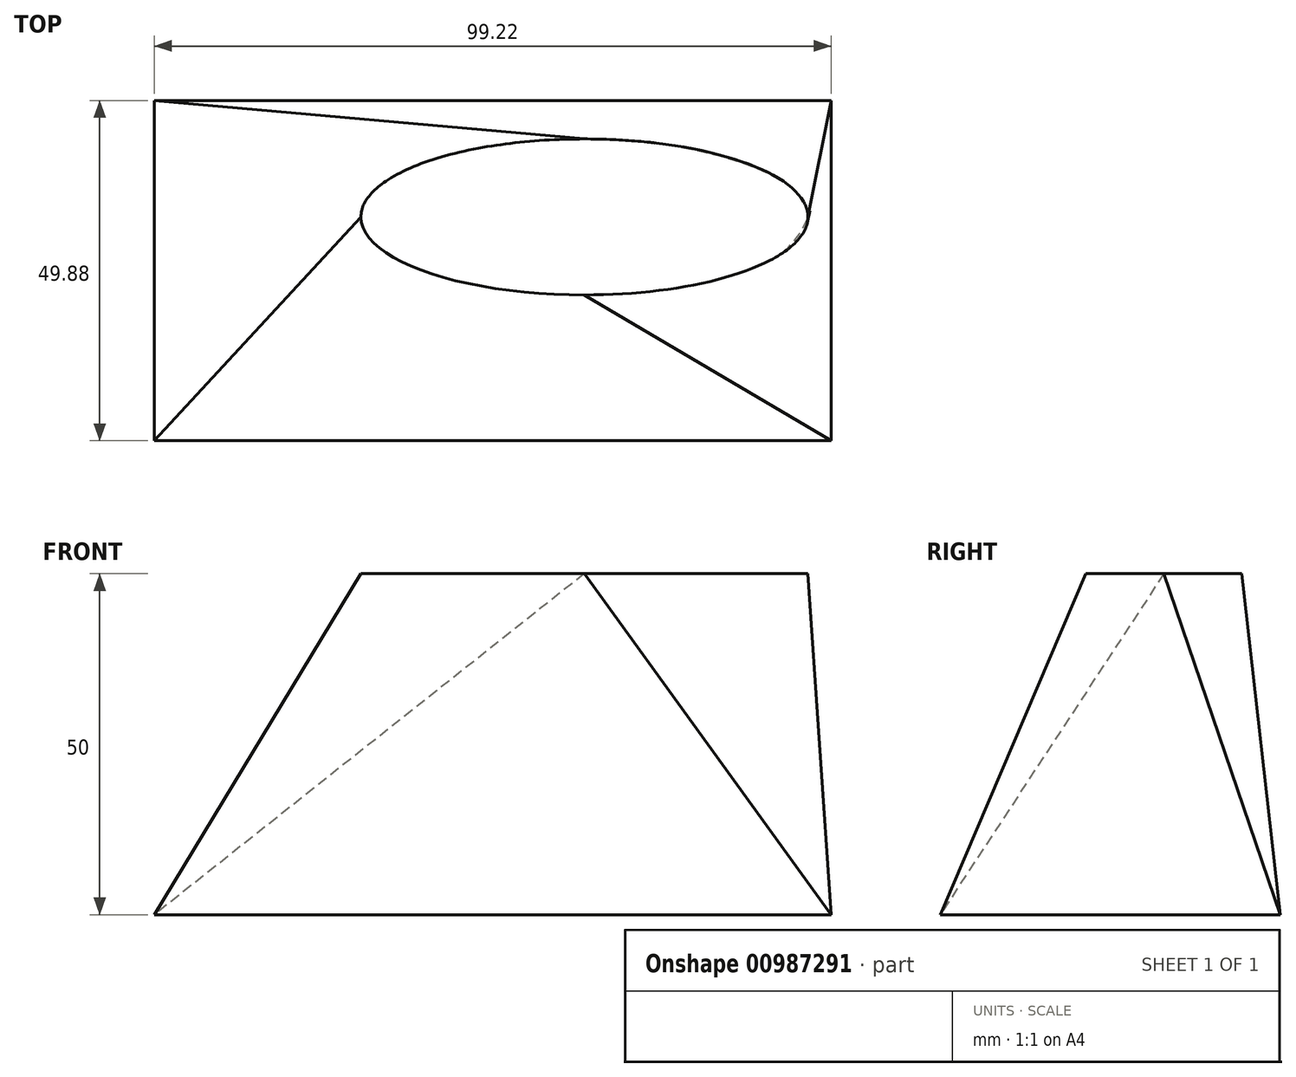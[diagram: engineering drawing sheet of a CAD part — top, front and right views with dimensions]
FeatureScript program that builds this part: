
annotation { "Feature Type Name" : "Feature", "Feature Type Description" : "" }
export const myFeature = defineFeature(function(context is Context, id is Id, definition is map)
    precondition{}
    {
        {
            var Q0;
            Q0=qCreatedBy(makeId("Top.planeOp"),FACE);
            var sketch = newSketch(context, id + "F0", { "sketchPlane" : qUnion([Q0])});
            skLineSegment(sketch, "E0.bottom", {"start": v(49.61, -24.94) * mm, "end": v(-49.61, -24.94) * mm});
            skLineSegment(sketch, "E0.top", {"start": v(49.61, 24.94) * mm, "end": v(-49.61, 24.94) * mm});
            skLineSegment(sketch, "E0.left", {"start": v(49.61, -24.94) * mm, "end": v(49.61, 24.94) * mm});
            skLineSegment(sketch, "E0.right", {"start": v(-49.61, -24.94) * mm, "end": v(-49.61, 24.94) * mm});
            skPoint(sketch, "E0.middle", {"position": v(0, 0) * mm});
            skSolve(sketch);
        }
        {
            var Q0;
            Q0=qCreatedBy(makeId("Top.planeOp"),FACE);
            cPlane(context, id + "F1", {"entities" : qUnion([Q0]), "cplaneType" : CPlaneType.OFFSET, "offset" : 50 * mm, "width" : 150 * mm, "height" : 150 * mm});
        }
        {
            var Q0;
            Q0=qCreatedBy(id+"F1.planeOp",FACE);
            var sketch = newSketch(context, id + "F2", { "sketchPlane" : qUnion([Q0])});
            skEllipticalArc(sketch, "E1", {});
            skEllipticalArc(sketch, "E2", {});
            skEllipticalArc(sketch, "E3", {});
            skEllipticalArc(sketch, "E4", {});
            const initialGuessF2  = {"E1": [0.013439871370792389, 0.007863917388021946, 1, 0, 0.03277255967259407, 0.011433524307446563, 3.141592653589793, 1.5707963267948966], "E2": [0.013439871370792389, 0.007863917388021946, 1, 0, 0.03277255967259407, 0.011433524307446563, 0, 3.141592653589793], "E3": [0.013439871370792389, 0.007863917388021946, 1, 0, 0.03277255967259407, 0.011433524307446563, 4.71238898038469, 0], "E4": [0.013439871370792389, 0.007863917388021946, 1, 0, 0.03277255967259407, 0.011433524307446563, 1.5707963267948966, 4.71238898038469]};
            skSetInitialGuess(sketch, initialGuessF2);
            skSolve(sketch);
        }
        {
            var Q0;
            Q0=makeQuery(id+"F2.imprint","IMPRINT",FACE,{"disambiguationData":[TD([[makeQuery(id+"F2.imprint","IMPRINT",EDGE,{"derivedFrom":sQuery(id+"F2.wireOp",EDGE,"E2")}),1.0]])]});
            var Q1;
            Q1=makeQuery(id+"F0.imprint","IMPRINT",FACE,{"disambiguationData":[TD([[makeQuery(id+"F0.imprint","IMPRINT",EDGE,{"derivedFrom":sQuery(id+"F0.wireOp",EDGE,"E0.bottom")}),-1.0]])]});
            var Q2;
            Q2=sQuery(id+"F0.wireOp",VERTEX,"E0.bottom.end");
            var Q3;
            Q3=sQuery(id+"F2.wireOp",VERTEX,"E1.start");
            loft(context, id + "F3", {"sheetProfilesArray" : [{ "sheetProfileEntities" : qUnion([Q0]) }, { "sheetProfileEntities" : qUnion([Q1]) }], "matchConnections" : true, "connections" : [{ "connectionEntities" : qUnion([Q2, Q3]), "connectionEdgeQueries" : qUnion([]), "connectionEdgeParameters" : [] }]});
        }
    });
